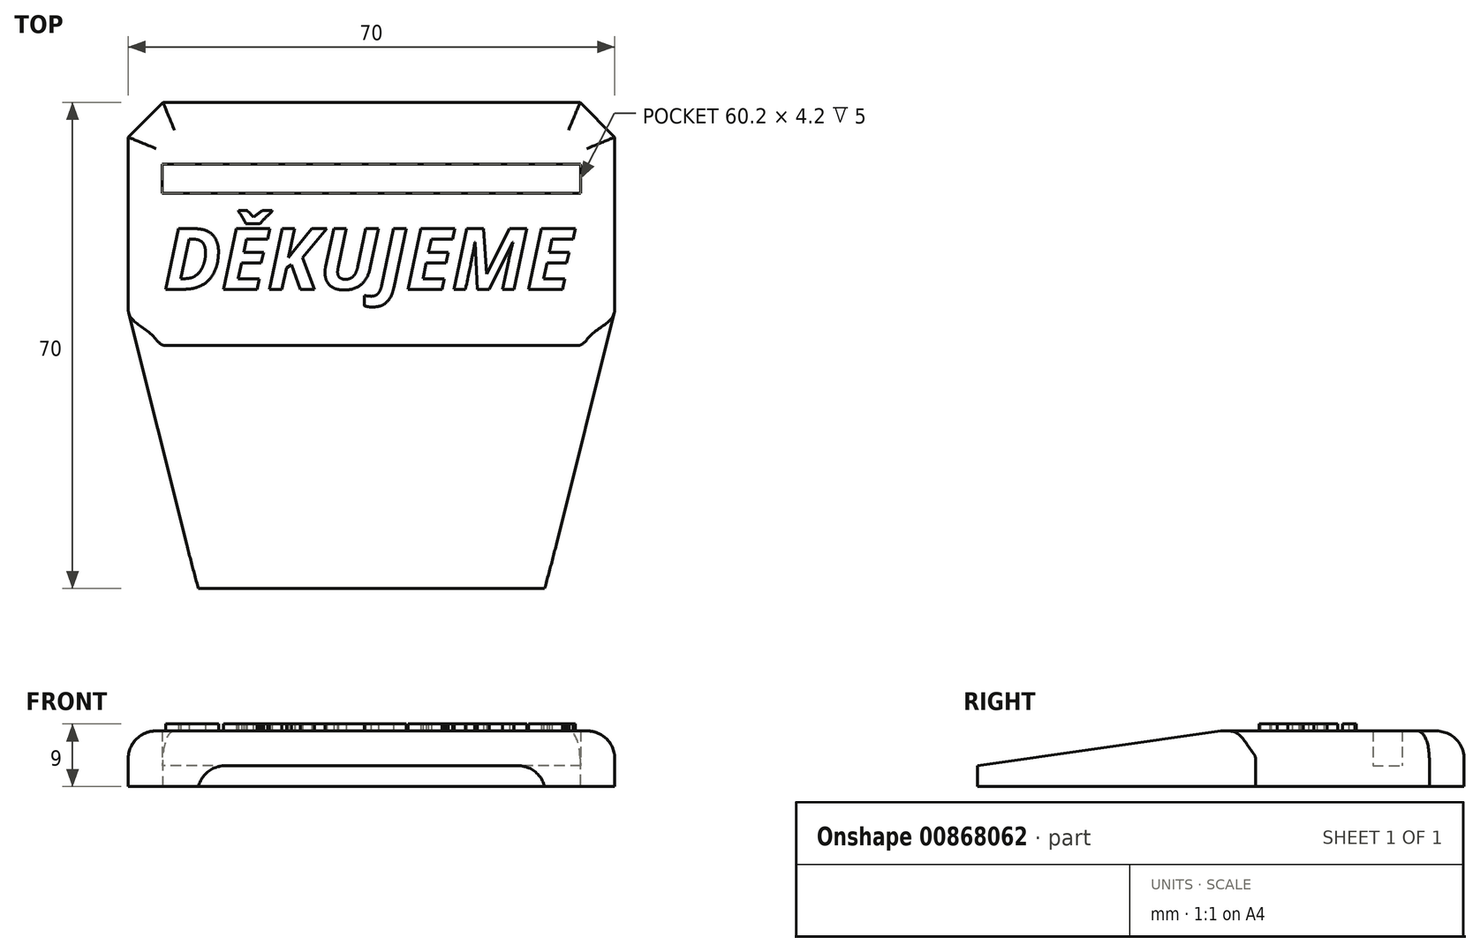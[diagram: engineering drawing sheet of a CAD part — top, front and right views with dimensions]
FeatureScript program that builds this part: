
annotation { "Feature Type Name" : "Feature", "Feature Type Description" : "" }
export const myFeature = defineFeature(function(context is Context, id is Id, definition is map)
    precondition{}
    {
        {
            var Q0;
            Q0=qCreatedBy(makeId("Top.planeOp"),FACE);
            var sketch = newSketch(context, id + "F0", { "sketchPlane" : qUnion([Q0])});
            skLineSegment(sketch, "E0.bottom", {"start": v(35, -35) * mm, "end": v(-35, -35) * mm});
            skLineSegment(sketch, "E0.top", {"start": v(35, 35) * mm, "end": v(-35, 35) * mm});
            skLineSegment(sketch, "E0.left", {"start": v(35, -35) * mm, "end": v(35, 35) * mm});
            skLineSegment(sketch, "E0.right", {"start": v(-35, -35) * mm, "end": v(-35, 35) * mm});
            skPoint(sketch, "E0.middle", {"position": v(0, 0) * mm});
            skLineSegment(sketch, "E1.bottom", {"start": v(30.1, 21.9) * mm, "end": v(-30.1, 21.9) * mm});
            skLineSegment(sketch, "E1.top", {"start": v(30.1, 26.1) * mm, "end": v(-30.1, 26.1) * mm});
            skLineSegment(sketch, "E1.left", {"start": v(30.1, 21.9) * mm, "end": v(30.1, 26.1) * mm});
            skLineSegment(sketch, "E1.right", {"start": v(-30.1, 21.9) * mm, "end": v(-30.1, 26.1) * mm});
            skPoint(sketch, "E1.middle", {"position": v(0, 24) * mm});
            skSolve(sketch);
        }
        {
            var Q0;
            Q0=makeQuery(id+"F0.imprint","IMPRINT",FACE,{"disambiguationData":[TD([[makeQuery(id+"F0.imprint","IMPRINT",EDGE,{"derivedFrom":sQuery(id+"F0.wireOp",EDGE,"E0.bottom")}),-1.0]])]});
            extrude(context, id + "F1", {"entities" : qUnion([Q0]), "depth" : 8 * mm, "offsetDistance" : 25 * mm});
        }
        {
            var Q0;
            Q0=makeQuery(id+"F0.imprint","IMPRINT",FACE,{"disambiguationData":[TD([[makeQuery(id+"F0.imprint","IMPRINT",EDGE,{"derivedFrom":sQuery(id+"F0.wireOp",EDGE,"E1.bottom")}),-1.0]])]});
            extrude(context, id + "F2", {"entities" : qUnion([Q0]), "operationType" : NewBodyOperationType.ADD, "depth" : 3 * mm, "offsetDistance" : 25 * mm});
        }
        {
            var Q0;
            Q0=makeQuery(id+"F1.opExtrude","SWEPT_EDGE",EDGE,{"disambiguationData":[OSD([sQuery(id+"F0.wireOp",EDGE,"E0.top"),sQuery(id+"F0.wireOp",EDGE,"E0.right")])]});
            var Q1;
            Q1=makeQuery(id+"F1.opExtrude","SWEPT_EDGE",EDGE,{"disambiguationData":[OSD([sQuery(id+"F0.wireOp",EDGE,"E0.top"),sQuery(id+"F0.wireOp",EDGE,"E0.left")])]});
            chamfer(context, id + "F3", {"entities" : qUnion([Q0, Q1]), "width" : 5 * mm, "tangentPropagation" : true});
        }
        {
            var Q0;
            Q0=makeQuery(id+"F1.opExtrude","SWEPT_EDGE",EDGE,{"disambiguationData":[OSD([sQuery(id+"F0.wireOp",EDGE,"E0.bottom"),sQuery(id+"F0.wireOp",EDGE,"E0.right")])]});
            var Q1;
            Q1=makeQuery(id+"F1.opExtrude","SWEPT_EDGE",EDGE,{"disambiguationData":[OSD([sQuery(id+"F0.wireOp",EDGE,"E0.bottom"),sQuery(id+"F0.wireOp",EDGE,"E0.left")])]});
            chamfer(context, id + "F4", {"entities" : qUnion([Q0, Q1]), "chamferType" : ChamferType.TWO_OFFSETS, "width1" : 10 * mm, "oppositeDirection" : false, "width2" : 40 * mm, "tangentPropagation" : true});
        }
        {
            var Q0;
            Q0=makeQuery(id+"F1.opExtrude","CAP_EDGE",EDGE,{"disambiguationData":[OSD([sQuery(id+"F0.wireOp",EDGE,"E0.bottom")])],"isStart":false});
            chamfer(context, id + "F5", {"entities" : qUnion([Q0]), "chamferType" : ChamferType.TWO_OFFSETS, "width1" : 5 * mm, "oppositeDirection" : false, "width2" : 35 * mm, "tangentPropagation" : true});
        }
        {
            var Q0;
            {var subQ0=sQuery(id+"F0.wireOp",EDGE,"E0.right");var subQ1=sQuery(id+"F0.wireOp",EDGE,"E0.top");Q0=makeQuery(id+"F3.opChamfer","BLEND_EDGE",EDGE,{"blendedFrom":[makeQuery(id+"F1.opExtrude","SWEPT_EDGE",EDGE,{"disambiguationData":[OSD([subQ1,subQ0])]}),makeQuery(id+"F1.opExtrude","CAP_FACE",FACE,{"disambiguationData":[OSD([sQuery(id+"F0.wireOp",EDGE,"E0.bottom"),subQ1,sQuery(id+"F0.wireOp",EDGE,"E0.left"),subQ0,sQuery(id+"F0.wireOp",EDGE,"E1.bottom"),sQuery(id+"F0.wireOp",EDGE,"E1.top"),sQuery(id+"F0.wireOp",EDGE,"E1.left"),sQuery(id+"F0.wireOp",EDGE,"E1.right")])],"isStart":false})],"blendedInto":[makeQuery(id+"F1.opExtrude","CAP_FACE",FACE,{"disambiguationData":[OSD([sQuery(id+"F0.wireOp",EDGE,"E0.bottom"),subQ1,sQuery(id+"F0.wireOp",EDGE,"E0.left"),subQ0,sQuery(id+"F0.wireOp",EDGE,"E1.bottom"),sQuery(id+"F0.wireOp",EDGE,"E1.top"),sQuery(id+"F0.wireOp",EDGE,"E1.left"),sQuery(id+"F0.wireOp",EDGE,"E1.right")])],"isStart":false})]});}
            var Q1;
            Q1=makeQuery(id+"F1.opExtrude","CAP_EDGE",EDGE,{"disambiguationData":[OSD([sQuery(id+"F0.wireOp",EDGE,"E0.right")])],"isStart":false});
            var Q2;
            {var subQ0=sQuery(id+"F0.wireOp",EDGE,"E0.left");var subQ1=sQuery(id+"F0.wireOp",EDGE,"E0.top");Q2=makeQuery(id+"F3.opChamfer","BLEND_EDGE",EDGE,{"blendedFrom":[makeQuery(id+"F1.opExtrude","SWEPT_EDGE",EDGE,{"disambiguationData":[OSD([subQ1,subQ0])]}),makeQuery(id+"F1.opExtrude","CAP_FACE",FACE,{"disambiguationData":[OSD([sQuery(id+"F0.wireOp",EDGE,"E0.bottom"),subQ1,subQ0,sQuery(id+"F0.wireOp",EDGE,"E0.right"),sQuery(id+"F0.wireOp",EDGE,"E1.bottom"),sQuery(id+"F0.wireOp",EDGE,"E1.top"),sQuery(id+"F0.wireOp",EDGE,"E1.left"),sQuery(id+"F0.wireOp",EDGE,"E1.right")])],"isStart":false})],"blendedInto":[makeQuery(id+"F1.opExtrude","CAP_FACE",FACE,{"disambiguationData":[OSD([sQuery(id+"F0.wireOp",EDGE,"E0.bottom"),subQ1,subQ0,sQuery(id+"F0.wireOp",EDGE,"E0.right"),sQuery(id+"F0.wireOp",EDGE,"E1.bottom"),sQuery(id+"F0.wireOp",EDGE,"E1.top"),sQuery(id+"F0.wireOp",EDGE,"E1.left"),sQuery(id+"F0.wireOp",EDGE,"E1.right")])],"isStart":false})]});}
            var Q3;
            Q3=makeQuery(id+"F1.opExtrude","CAP_EDGE",EDGE,{"disambiguationData":[OSD([sQuery(id+"F0.wireOp",EDGE,"E0.top")])],"isStart":false});
            var Q4;
            Q4=makeQuery(id+"F1.opExtrude","CAP_EDGE",EDGE,{"disambiguationData":[OSD([sQuery(id+"F0.wireOp",EDGE,"E0.left")])],"isStart":false});
            var Q5;
            {var subQ0=sQuery(id+"F0.wireOp",EDGE,"E0.bottom");Q5=makeQuery(id+"F5.opChamfer","BLEND_EDGE",EDGE,{"blendedFrom":[makeQuery(id+"F1.opExtrude","CAP_EDGE",EDGE,{"disambiguationData":[OSD([subQ0])],"isStart":false}),makeQuery(id+"F4.opChamfer","BLEND_FACE",FACE,{"disambiguationData":[OSD([subQ0,sQuery(id+"F0.wireOp",EDGE,"E0.right")])]})],"blendedInto":[makeQuery(id+"F4.opChamfer","BLEND_FACE",FACE,{"disambiguationData":[OSD([subQ0,sQuery(id+"F0.wireOp",EDGE,"E0.right")])]})]});}
            var Q6;
            {var subQ0=sQuery(id+"F0.wireOp",EDGE,"E0.bottom");Q6=makeQuery(id+"F5.opChamfer","BLEND_EDGE",EDGE,{"blendedFrom":[makeQuery(id+"F1.opExtrude","CAP_EDGE",EDGE,{"disambiguationData":[OSD([subQ0])],"isStart":false}),makeQuery(id+"F4.opChamfer","BLEND_FACE",FACE,{"disambiguationData":[OSD([subQ0,sQuery(id+"F0.wireOp",EDGE,"E0.left")])]})],"blendedInto":[makeQuery(id+"F4.opChamfer","BLEND_FACE",FACE,{"disambiguationData":[OSD([subQ0,sQuery(id+"F0.wireOp",EDGE,"E0.left")])]})]});}
            fillet(context, id + "F6", {"entities" : qUnion([Q0, Q1, Q2, Q3, Q4, Q5, Q6]), "tangentPropagation" : true, "radius" : 4 * mm, "defaultsChanged" : true, "vertexSettings" : [], "allowEdgeOverflow" : false});
        }
        {
            var Q0;
            Q0=makeQuery(id+"F1.opExtrude","CAP_FACE",FACE,{"disambiguationData":[OSD([sQuery(id+"F0.wireOp",EDGE,"E0.bottom"),sQuery(id+"F0.wireOp",EDGE,"E0.top"),sQuery(id+"F0.wireOp",EDGE,"E0.left"),sQuery(id+"F0.wireOp",EDGE,"E0.right"),sQuery(id+"F0.wireOp",EDGE,"E1.bottom"),sQuery(id+"F0.wireOp",EDGE,"E1.top"),sQuery(id+"F0.wireOp",EDGE,"E1.left"),sQuery(id+"F0.wireOp",EDGE,"E1.right")])],"isStart":false});
            var sketch = newSketch(context, id + "F7", { "sketchPlane" : qUnion([Q0])});
            skText(sketch, "E2", { "text": "DĚKUJEME", "fontName": "OpenSans-BoldItalic.ttf"});
            const initialGuessF7  = {"E2": [-0.0299, 0.0081, 1, 0, 0.00879]};
            skSetInitialGuess(sketch, initialGuessF7);
            skSolve(sketch);
        }
        {
            var Q0;
            Q0 = qSketchRegion(id + "F7", true);
            extrude(context, id + "F8", {"entities" : qUnion([Q0]), "operationType" : NewBodyOperationType.ADD, "depth" : 1 * mm, "offsetDistance" : 25 * mm});
        }
    });
